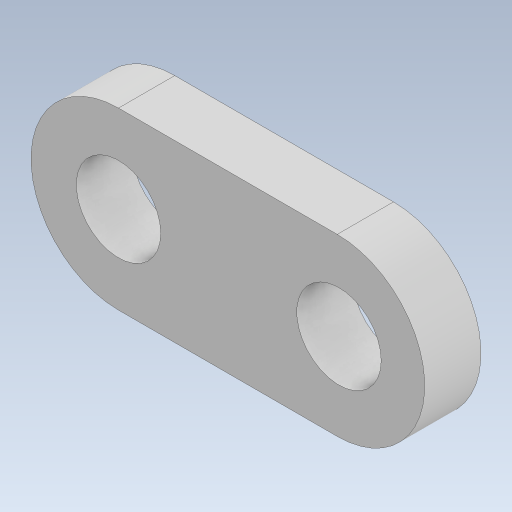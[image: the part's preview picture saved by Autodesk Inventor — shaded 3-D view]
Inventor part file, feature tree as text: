
AUTODESK INVENTOR PART (.ipt)
format: ipt  version: 2023 (Build 270158000, 158)  size: 299,520 bytes
history: native  units: in
note: dims shown in document units (in); Inventor stores cm internally (conversion verified against a paired STEP export)
features: sketch x2, extrude x1, hole x1, fillet x1
ambient origin geometry x8: Origin, YZ Plane, XZ Plane, XY Plane, X Axis, Y Axis, Z Axis, Center Point
bodies: Solid1 (feature_tree)
feature tree (5):
  extrude  "Extrusion1"  Depth=0.1772in
  hole  "Hole1"  [1 undecoded]
  fillet  "Fillet1"  Radius=0.5512in
  sketch  "Sketch2"  dims[d7=0.689in d8=0.1772in]
  sketch  "Sketch3"  dims[d9=0.2756in d11=0.2756in d12=0.5512in d13=0.0in d14=0.6945in d15=0.2756in d16=0.266in d17=0.2362in d18=0.507in d19=0.0787in d20=0.5635in d21=0.1969in d22=0.8108in d23=0.2756in]
note: 1 required parameter value undecoded (feature->parameter linkage not recoverable at this tier; creation-order binding heuristic only, values carry confidence <= 0.55)
